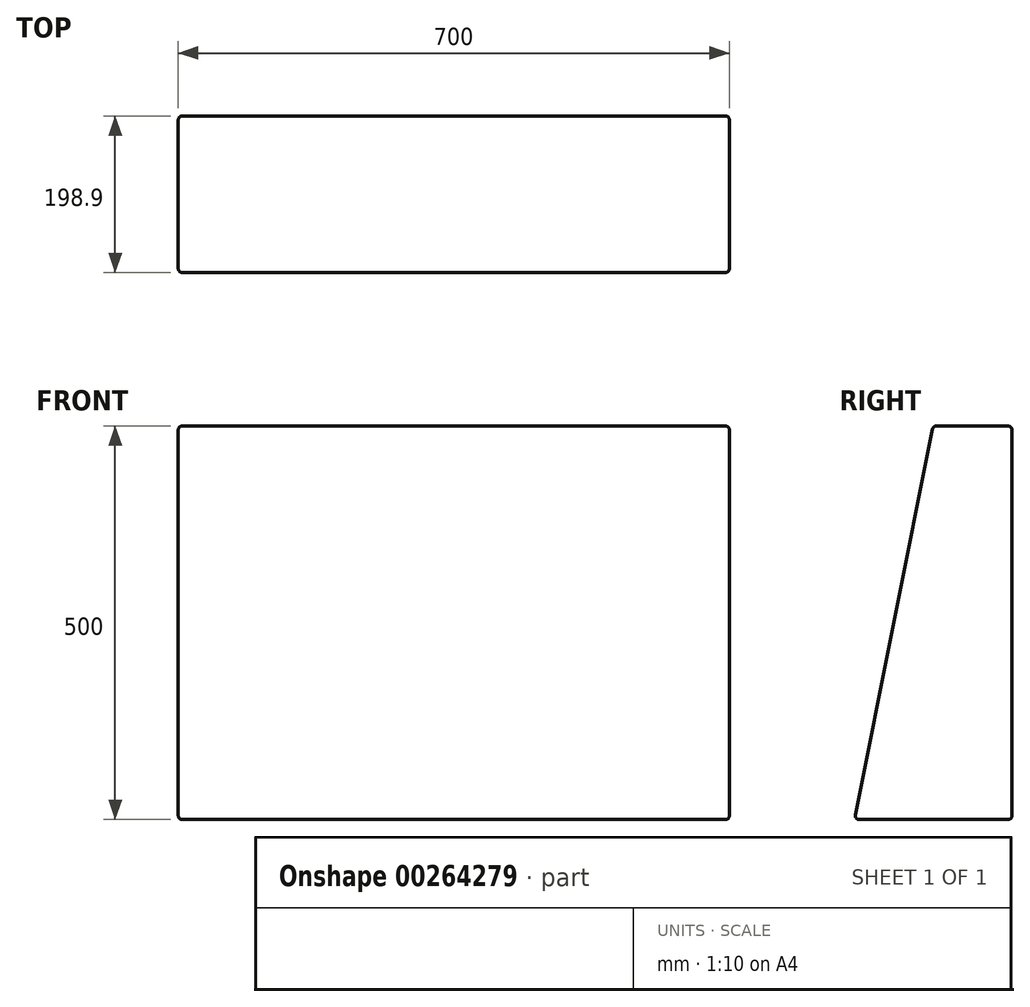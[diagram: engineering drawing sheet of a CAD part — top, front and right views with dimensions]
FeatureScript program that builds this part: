
annotation { "Feature Type Name" : "Feature", "Feature Type Description" : "" }
export const myFeature = defineFeature(function(context is Context, id is Id, definition is map)
    precondition{}
    {
        {
            var Q0;
            Q0=qCreatedBy(makeId("Right.planeOp"),FACE);
            var sketch = newSketch(context, id + "F0", { "sketchPlane" : qUnion([Q0])});
            skLineSegment(sketch, "E0", {"start": v(-50, 250) * mm, "end": v(50, 250) * mm});
            skLineSegment(sketch, "E1", {"start": v(50, 250) * mm, "end": v(50, -250) * mm});
            skLineSegment(sketch, "E2", {"start": v(50, -250) * mm, "end": v(-150, -250) * mm});
            skLineSegment(sketch, "E3", {"start": v(-150, -250) * mm, "end": v(-50, 250) * mm});
            skLineSegment(sketch, "E4", {"start": v(50, 0) * mm, "end": v(-100, 0) * mm, "construction": true});
            skLineSegment(sketch, "E5", {"start": v(0, 250) * mm, "end": v(0, -250) * mm, "construction": true});
            skSolve(sketch);
        }
        {
            var Q0;
            Q0=makeQuery(id+"F0.imprint","IMPRINT",FACE,{"disambiguationData":[TD([[makeQuery(id+"F0.imprint","IMPRINT",EDGE,{"derivedFrom":sQuery(id+"F0.wireOp",EDGE,"E0")}),-1.0]])]});
            extrude(context, id + "F1", {"entities" : qUnion([Q0]), "endBound" : BoundingType.SYMMETRIC, "depth" : 700 * mm});
        }
        {
            var Q0;
            Q0=makeQuery(id+"F1.opExtrude","CAP_EDGE",EDGE,{"disambiguationData":[OSD([sQuery(id+"F0.wireOp",EDGE,"E3")])],"isStart":true});
            var Q1;
            Q1=makeQuery(id+"F1.opExtrude","SWEPT_EDGE",EDGE,{"disambiguationData":[OSD([sQuery(id+"F0.wireOp",EDGE,"E0"),sQuery(id+"F0.wireOp",EDGE,"E3")])]});
            var Q2;
            Q2=makeQuery(id+"F1.opExtrude","CAP_EDGE",EDGE,{"disambiguationData":[OSD([sQuery(id+"F0.wireOp",EDGE,"E3")])],"isStart":false});
            var Q3;
            Q3=makeQuery(id+"F1.opExtrude","SWEPT_EDGE",EDGE,{"disambiguationData":[OSD([sQuery(id+"F0.wireOp",EDGE,"E2"),sQuery(id+"F0.wireOp",EDGE,"E3")])]});
            var Q4;
            Q4=makeQuery(id+"F1.opExtrude","CAP_EDGE",EDGE,{"disambiguationData":[OSD([sQuery(id+"F0.wireOp",EDGE,"E0")])],"isStart":true});
            var Q5;
            Q5=makeQuery(id+"F1.opExtrude","CAP_EDGE",EDGE,{"disambiguationData":[OSD([sQuery(id+"F0.wireOp",EDGE,"E0")])],"isStart":false});
            var Q6;
            Q6=makeQuery(id+"F1.opExtrude","CAP_EDGE",EDGE,{"disambiguationData":[OSD([sQuery(id+"F0.wireOp",EDGE,"E2")])],"isStart":false});
            var Q7;
            Q7=makeQuery(id+"F1.opExtrude","CAP_EDGE",EDGE,{"disambiguationData":[OSD([sQuery(id+"F0.wireOp",EDGE,"E1")])],"isStart":false});
            var Q8;
            Q8=makeQuery(id+"F1.opExtrude","SWEPT_EDGE",EDGE,{"disambiguationData":[OSD([sQuery(id+"F0.wireOp",EDGE,"E0"),sQuery(id+"F0.wireOp",EDGE,"E1")])]});
            var Q9;
            Q9=makeQuery(id+"F1.opExtrude","CAP_FACE",FACE,{"disambiguationData":[OSD([sQuery(id+"F0.wireOp",EDGE,"E0"),sQuery(id+"F0.wireOp",EDGE,"E1"),sQuery(id+"F0.wireOp",EDGE,"E2"),sQuery(id+"F0.wireOp",EDGE,"E3")])],"isStart":true});
            var Q10;
            Q10=makeQuery(id+"F1.opExtrude","CAP_EDGE",EDGE,{"disambiguationData":[OSD([sQuery(id+"F0.wireOp",EDGE,"E1")])],"isStart":true});
            var Q11;
            Q11=makeQuery(id+"F1.opExtrude","SWEPT_EDGE",EDGE,{"disambiguationData":[OSD([sQuery(id+"F0.wireOp",EDGE,"E1"),sQuery(id+"F0.wireOp",EDGE,"E2")])]});
            fillet(context, id + "F2", {"entities" : qUnion([Q0, Q1, Q2, Q3, Q4, Q5, Q6, Q7, Q8, Q9, Q10, Q11]), "radius" : 5 * mm, "tangentPropagation" : true, "allowEdgeOverflow" : false});
        }
    });
